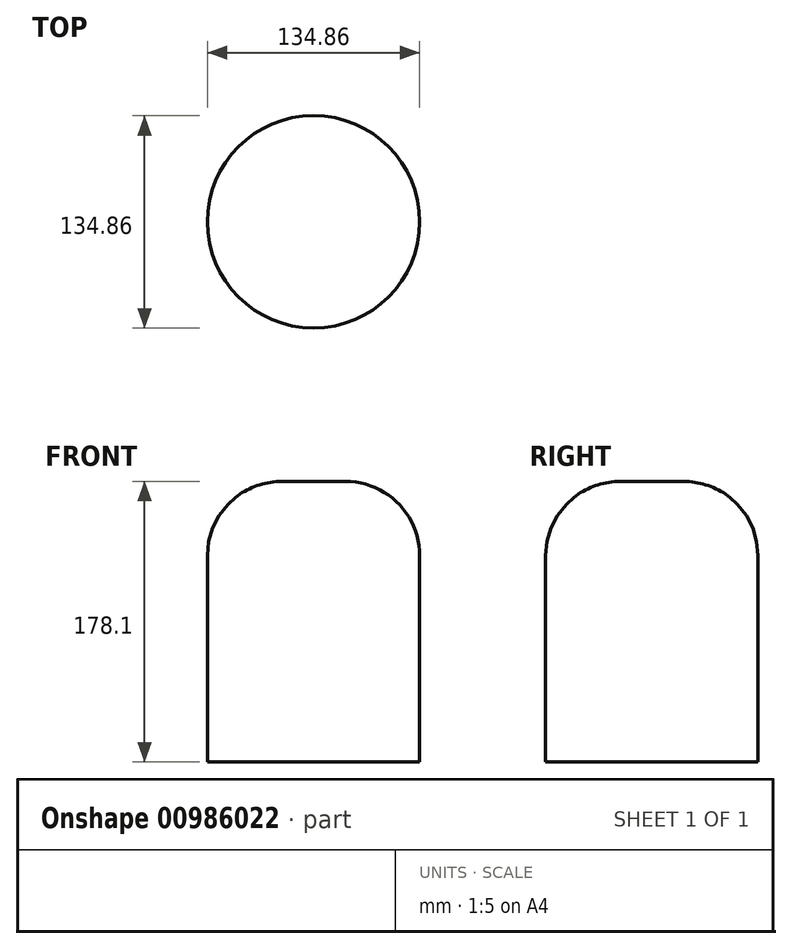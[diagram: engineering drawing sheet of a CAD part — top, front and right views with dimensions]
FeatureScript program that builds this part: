
annotation { "Feature Type Name" : "Feature", "Feature Type Description" : "" }
export const myFeature = defineFeature(function(context is Context, id is Id, definition is map)
    precondition{}
    {
        {
            var Q0;
            Q0=qCreatedBy(makeId("Top.planeOp"),FACE);
            var sketch = newSketch(context, id + "F0", { "sketchPlane" : qUnion([Q0])});
            skCircle(sketch, "E0", {"center": v(0, 0) * mm, "radius": 67.43 * mm});
            skSolve(sketch);
        }
        {
            var Q0;
            Q0=makeQuery(id+"F0.imprint","IMPRINT",FACE,{"disambiguationData":[TD([[makeQuery(id+"F0.imprint","IMPRINT",EDGE,{"derivedFrom":sQuery(id+"F0.wireOp",EDGE,"E0")}),1.0]])]});
            var sketch = newSketch(context, id + "F1", { "sketchPlane" : qUnion([Q0])});
            skSolve(sketch);
        }
        {
            var Q0;
            Q0=makeQuery(id+"F1.imprint","IMPRINT",FACE,{"disambiguationData":[TD([[makeQuery(id+"F1.imprint","IMPRINT",EDGE,{"derivedFrom":makeQuery(id+"F0.imprint","IMPRINT",EDGE,{"derivedFrom":sQuery(id+"F0.wireOp",EDGE,"E0")})}),1.0]])]});
            var sketch = newSketch(context, id + "F2", { "sketchPlane" : qUnion([Q0])});
            skSolve(sketch);
        }
        {
            var Q0;
            Q0=makeQuery(id+"F2.imprint","IMPRINT",FACE,{"disambiguationData":[TD([[makeQuery(id+"F2.imprint","IMPRINT",EDGE,{"derivedFrom":makeQuery(id+"F1.imprint","IMPRINT",EDGE,{"derivedFrom":makeQuery(id+"F0.imprint","IMPRINT",EDGE,{"derivedFrom":sQuery(id+"F0.wireOp",EDGE,"E0")})})}),1.0]])]});
            extrude(context, id + "F3", {"entities" : qUnion([Q0]), "depth" : 178.1 * mm, "offsetDistance" : 25.4 * mm});
        }
        {
            var Q0;
            Q0=makeQuery(id+"F3.opExtrude","CAP_FACE",FACE,{"disambiguationData":[OSD([sQuery(id+"F0.wireOp",EDGE,"E0")])],"isStart":false});
            fillet(context, id + "F4", {"entities" : qUnion([Q0]), "radius" : 47.03 * mm, "tangentPropagation" : true, "allowEdgeOverflow" : false});
        }
    });
